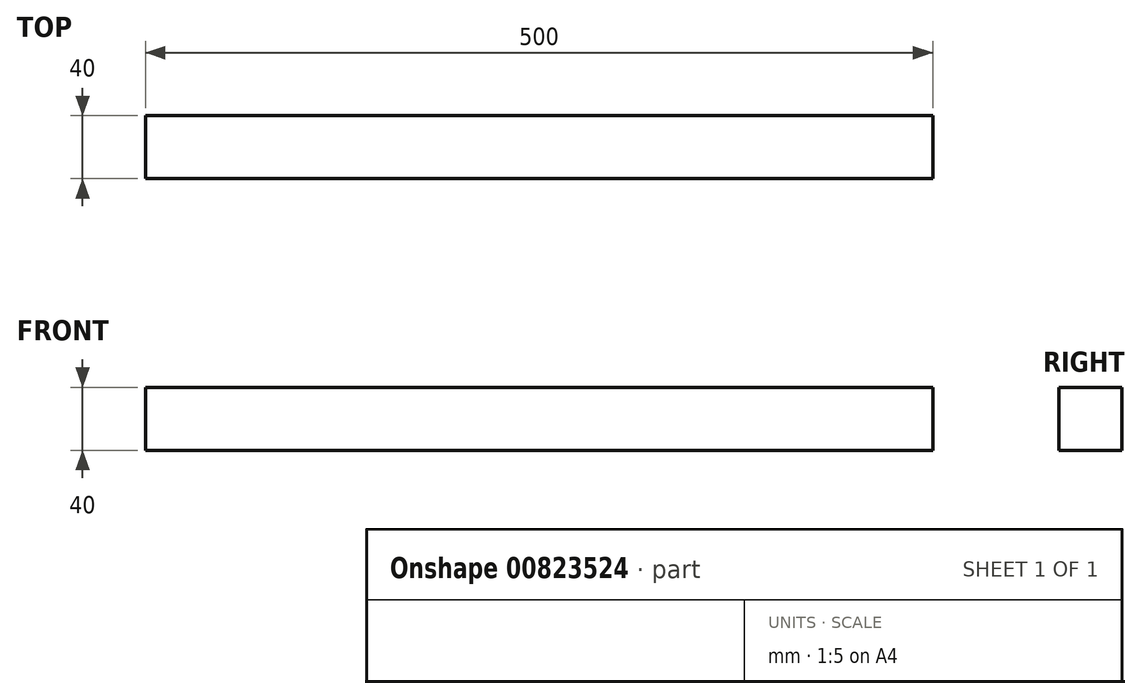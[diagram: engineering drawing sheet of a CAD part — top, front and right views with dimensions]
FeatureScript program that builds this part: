
annotation { "Feature Type Name" : "Feature", "Feature Type Description" : "" }
export const myFeature = defineFeature(function(context is Context, id is Id, definition is map)
    precondition{}
    {
        {
            var Q0;
            Q0=qCreatedBy(makeId("Front.planeOp"),FACE);
            var sketch = newSketch(context, id + "F0", { "sketchPlane" : qUnion([Q0])});
            skLineSegment(sketch, "E0.bottom", {"start": v(250, -20) * mm, "end": v(-250, -20) * mm});
            skLineSegment(sketch, "E0.top", {"start": v(250, 20) * mm, "end": v(-250, 20) * mm});
            skLineSegment(sketch, "E0.left", {"start": v(250, -20) * mm, "end": v(250, 20) * mm});
            skLineSegment(sketch, "E0.right", {"start": v(-250, -20) * mm, "end": v(-250, 20) * mm});
            skPoint(sketch, "E0.middle", {"position": v(0, 0) * mm});
            skSolve(sketch);
        }
        {
            var Q0;
            Q0 = qSketchRegion(id + "F0", true);
            extrude(context, id + "F1", {"entities" : qUnion([Q0]), "depth" : 40 * mm, "offsetDistance" : 25 * mm});
        }
    });
